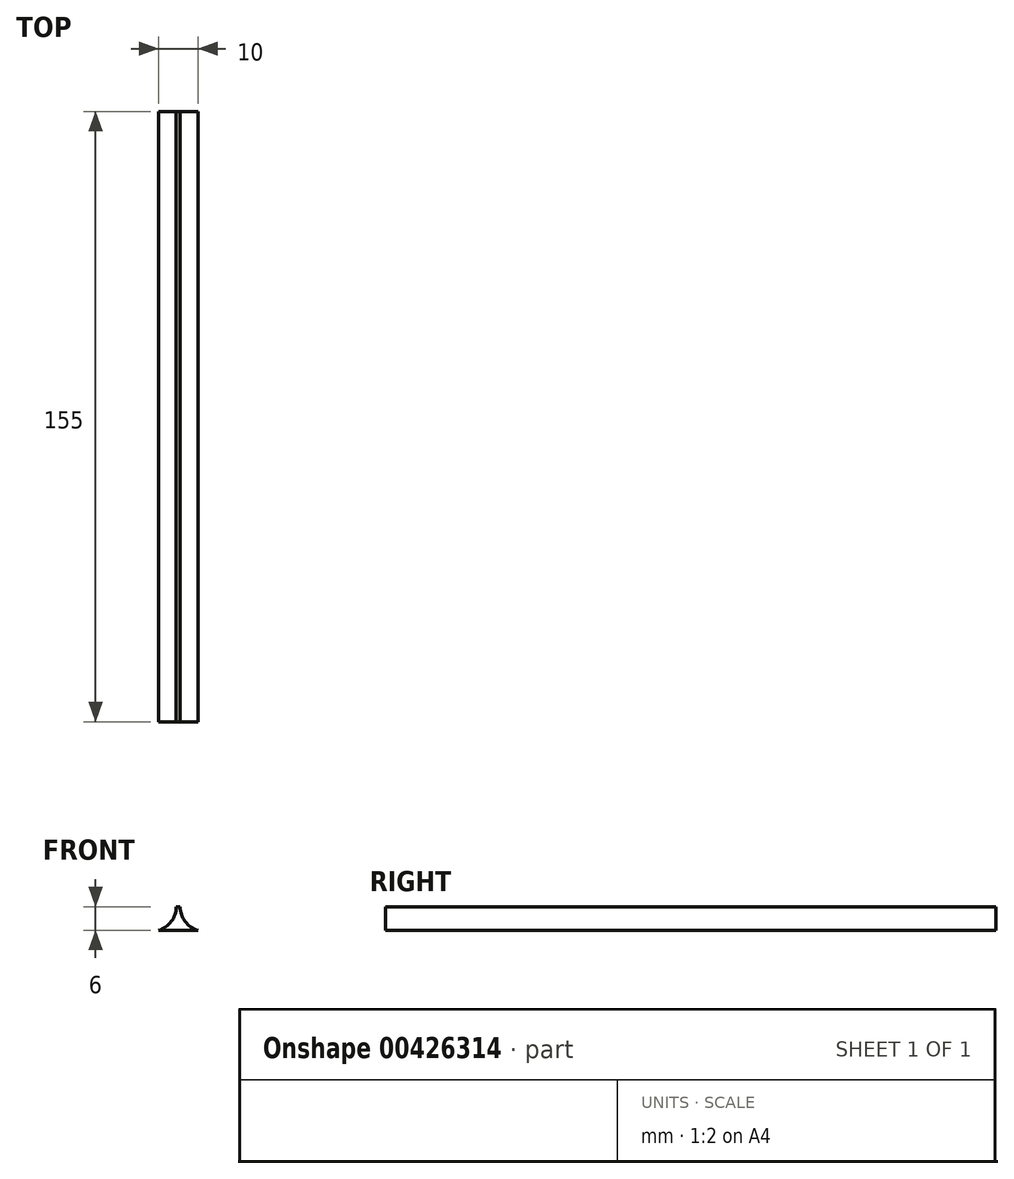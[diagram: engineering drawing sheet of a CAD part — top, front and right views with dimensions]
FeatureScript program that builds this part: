
annotation { "Feature Type Name" : "Feature", "Feature Type Description" : "" }
export const myFeature = defineFeature(function(context is Context, id is Id, definition is map)
    precondition{}
    {
        {
            var Q0;
            Q0=qCreatedBy(makeId("Front.planeOp"),FACE);
            var sketch = newSketch(context, id + "F0", { "sketchPlane" : qUnion([Q0])});
            skArc(sketch, "E0", {"start": v(0.5, 6) * mm, "mid": v(1.75, 2.25) * mm, "end": v(5, 0) * mm});
            skLineSegment(sketch, "E1", {"start": v(0, 6) * mm, "end": v(0.5, 6) * mm});
            skLineSegment(sketch, "E2", {"start": v(0, 0) * mm, "end": v(5, 0) * mm});
            skLineSegment(sketch, "E3.MirrorCS", {"start": v(0, 6) * mm, "end": v(-0.5, 6) * mm});
            skArc(sketch, "E4.MirrorCS", {"start": v(-0.5, 6) * mm, "mid": v(-1.75, 2.25) * mm, "end": v(-5, 0) * mm});
            skLineSegment(sketch, "E5.MirrorCS", {"start": v(0, 0) * mm, "end": v(-5, 0) * mm});
            skSolve(sketch);
        }
        {
            var Q0;
            Q0=qSketchRegion(id+"F0",true);
            extrude(context, id + "F1", {"entities" : qUnion([Q0]), "depth" : 155 * mm, "offsetDistance" : 25 * mm});
        }
    });
